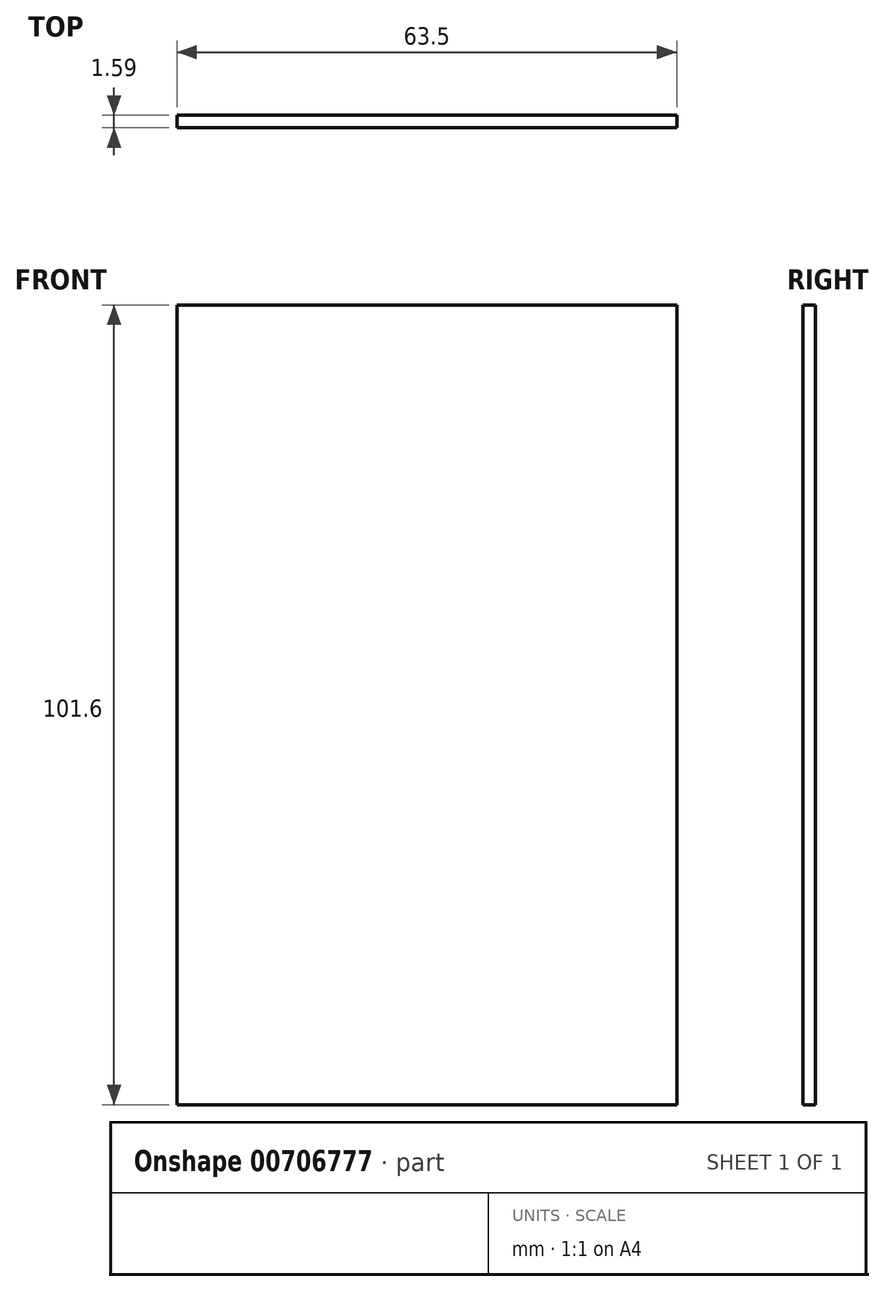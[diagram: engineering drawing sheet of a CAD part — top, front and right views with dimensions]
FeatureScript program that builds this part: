
annotation { "Feature Type Name" : "Feature", "Feature Type Description" : "" }
export const myFeature = defineFeature(function(context is Context, id is Id, definition is map)
    precondition{}
    {
        {
            var Q0;
            Q0=qCreatedBy(makeId("Front.planeOp"),FACE);
            var sketch = newSketch(context, id + "F0", { "sketchPlane" : qUnion([Q0])});
            skLineSegment(sketch, "E0.bottom", {"start": v(-63.5, 0) * mm, "end": v(0, 0) * mm});
            skLineSegment(sketch, "E0.top", {"start": v(-63.5, -101.6) * mm, "end": v(0, -101.6) * mm});
            skLineSegment(sketch, "E0.left", {"start": v(-63.5, 0) * mm, "end": v(-63.5, -101.6) * mm});
            skLineSegment(sketch, "E0.right", {"start": v(0, 0) * mm, "end": v(0, -101.6) * mm});
            skSolve(sketch);
        }
        {
            var Q0;
            Q0 = qSketchRegion(id + "F0", true);
            extrude(context, id + "F1", {"entities" : qUnion([Q0]), "depth" : 1.59 * mm, "offsetDistance" : 25.4 * mm});
        }
    });
